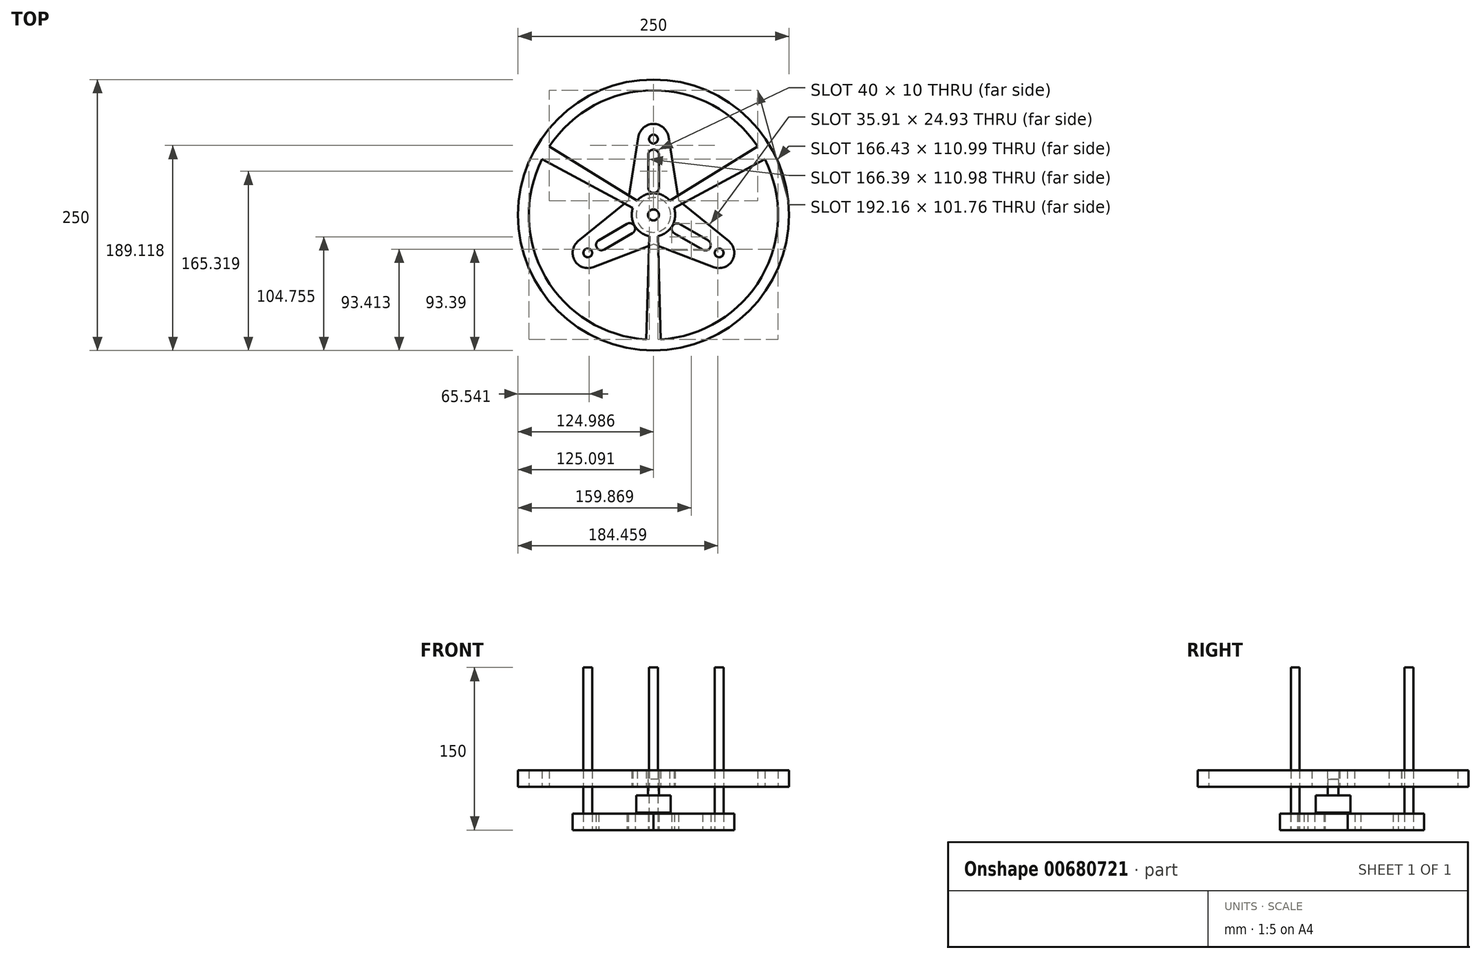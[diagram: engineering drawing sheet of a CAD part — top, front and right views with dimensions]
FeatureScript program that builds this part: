
annotation { "Feature Type Name" : "Feature", "Feature Type Description" : "" }
export const myFeature = defineFeature(function(context is Context, id is Id, definition is map)
    precondition{}
    {
        {
            var Q0;
            Q0=qCreatedBy(makeId("Top.planeOp"),FACE);
            var sketch = newSketch(context, id + "F0", { "sketchPlane" : qUnion([Q0])});
            skCircle(sketch, "E0", {"center": v(0, 70) * mm, "radius": 4 * mm});
            skCircle(sketch, "E1.1.0", {"center": v(-60.62, -35) * mm, "radius": 4 * mm});
            skCircle(sketch, "E1.2.0", {"center": v(60.62, -35) * mm, "radius": 4 * mm});
            skPoint(sketch, "E1.center", {"position": v(0, 0) * mm});
            skSolve(sketch);
        }
        {
            var Q0;
            Q0=makeQuery(id+"F0.imprint","IMPRINT",FACE,{"disambiguationData":[TD([[makeQuery(id+"F0.imprint","IMPRINT",EDGE,{"derivedFrom":sQuery(id+"F0.wireOp",EDGE,"E0")}),1.0]])]});
            var Q1;
            Q1=makeQuery(id+"F0.imprint","IMPRINT",FACE,{"disambiguationData":[TD([[makeQuery(id+"F0.imprint","IMPRINT",EDGE,{"derivedFrom":sQuery(id+"F0.wireOp",EDGE,"E1.1.0")}),1.0]])]});
            var Q2;
            Q2=makeQuery(id+"F0.imprint","IMPRINT",FACE,{"disambiguationData":[TD([[makeQuery(id+"F0.imprint","IMPRINT",EDGE,{"derivedFrom":sQuery(id+"F0.wireOp",EDGE,"E1.2.0")}),1.0]])]});
            extrude(context, id + "F1", {"entities" : qUnion([Q0, Q1, Q2]), "depth" : 150 * mm, "offsetDistance" : 25 * mm});
        }
        {
            var Q0;
            Q0=qCreatedBy(makeId("Top.planeOp"),FACE);
            var sketch = newSketch(context, id + "F2", { "sketchPlane" : qUnion([Q0])});
            skCircle(sketch, "E2", {"center": v(0, 0) * mm, "radius": 25 * mm});
            skCircle(sketch, "E3", {"center": v(0, 70) * mm, "radius": 14 * mm});
            skLineSegment(sketch, "E4", {"start": v(13.83, 72.2) * mm, "end": v(24.69, 3.93) * mm});
            skCircle(sketch, "E5", {"center": v(0, 70) * mm, "radius": 4.1 * mm});
            skLineSegment(sketch, "E6.MirrorCS", {"start": v(-13.83, 72.2) * mm, "end": v(-24.69, 3.93) * mm});
            skCircle(sketch, "E7.1.0", {"center": v(-60.62, -35) * mm, "radius": 14 * mm});
            skCircle(sketch, "E7.1.1", {"center": v(-60.62, -35) * mm, "radius": 4.1 * mm});
            skLineSegment(sketch, "E7.1.2", {"start": v(-55.61, -48.07) * mm, "end": v(8.94, -23.35) * mm});
            skLineSegment(sketch, "E7.1.3", {"start": v(-69.44, -24.13) * mm, "end": v(-15.75, 19.42) * mm});
            skCircle(sketch, "E7.2.0", {"center": v(60.62, -35) * mm, "radius": 14 * mm});
            skCircle(sketch, "E7.2.1", {"center": v(60.62, -35) * mm, "radius": 4.1 * mm});
            skLineSegment(sketch, "E7.2.2", {"start": v(69.44, -24.13) * mm, "end": v(15.75, 19.42) * mm});
            skLineSegment(sketch, "E7.2.3", {"start": v(55.61, -48.07) * mm, "end": v(-8.94, -23.35) * mm});
            skLineSegment(sketch, "E8", {"start": v(5.1, 55.44) * mm, "end": v(5.1, 25.44) * mm});
            skLineSegment(sketch, "E9", {"start": v(-4.9, 55.32) * mm, "end": v(-4.9, 25.32) * mm});
            skArc(sketch, "E10", {"start": v(-4.9, 55.32) * mm, "mid": v(0.03, 60.32) * mm, "end": v(5.1, 55.44) * mm});
            skArc(sketch, "E11", {"start": v(-4.9, 25.32) * mm, "mid": v(0.15, 20.32) * mm, "end": v(5.1, 25.44) * mm});
            skLineSegment(sketch, "E12.1.0", {"start": v(-45.45, -31.91) * mm, "end": v(-19.47, -16.91) * mm});
            skLineSegment(sketch, "E12.1.1", {"start": v(-50.56, -23.31) * mm, "end": v(-24.58, -8.31) * mm});
            skArc(sketch, "E12.1.2", {"start": v(-19.47, -16.91) * mm, "mid": v(-17.67, -10.03) * mm, "end": v(-24.58, -8.31) * mm});
            skArc(sketch, "E12.1.3", {"start": v(-45.45, -31.91) * mm, "mid": v(-52.25, -30.13) * mm, "end": v(-50.56, -23.31) * mm});
            skLineSegment(sketch, "E12.2.0", {"start": v(50.36, -23.4) * mm, "end": v(24.38, -8.4) * mm});
            skLineSegment(sketch, "E12.2.1", {"start": v(45.47, -32.13) * mm, "end": v(19.49, -17.13) * mm});
            skArc(sketch, "E12.2.2", {"start": v(24.38, -8.4) * mm, "mid": v(17.52, -10.3) * mm, "end": v(19.49, -17.13) * mm});
            skArc(sketch, "E12.2.3", {"start": v(50.36, -23.4) * mm, "mid": v(52.22, -30.19) * mm, "end": v(45.47, -32.13) * mm});
            skSolve(sketch);
        }
        {
            var Q0;
            {var subQ5=sQuery(id+"F2.wireOp",EDGE,"E9");Q0=makeQuery(id+"F2.imprint","IMPRINT",FACE,{"disambiguationData":[TD([[makeQuery(id+"F2.imprint","IMPRINT",EDGE,{"derivedFrom":subQ5}),-1.0]])]});}
            var Q1;
            Q1=makeQuery(id+"F2.imprint","IMPRINT",FACE,{"disambiguationData":[TD([[makeQuery(id+"F2.imprint","IMPRINT",EDGE,{"derivedFrom":sQuery(id+"F2.wireOp",EDGE,"E5")}),-1.0]])]});
            var Q2;
            {var subQ11=sQuery(id+"F2.wireOp",EDGE,"E8");Q2=makeQuery(id+"F2.imprint","IMPRINT",FACE,{"disambiguationData":[TD([[makeQuery(id+"F2.imprint","IMPRINT",EDGE,{"derivedFrom":subQ11}),1.0]])]});}
            var Q3;
            {var subQ0=sQuery(id+"F2.wireOp",EDGE,"E2");var subQ9=makeQuery(id+"F2.imprint","INTERSECT",VERTEX,{"derivedFrom":[subQ0,sQuery(id+"F2.wireOp",EDGE,"E4")]});Q3=makeQuery(id+"F2.imprint","IMPRINT",FACE,{"disambiguationData":[TD([[makeQuery(id+"F2.imprint","IMPRINT",EDGE,{"disambiguationData":[TD([[subQ9,-1.0]])],"derivedFrom":subQ0}),1.0]])]});}
            var Q4;
            {var subQ11=sQuery(id+"F2.wireOp",EDGE,"E12.1.1");Q4=makeQuery(id+"F2.imprint","IMPRINT",FACE,{"disambiguationData":[TD([[makeQuery(id+"F2.imprint","IMPRINT",EDGE,{"derivedFrom":subQ11}),1.0]])]});}
            var Q5;
            Q5=makeQuery(id+"F2.imprint","IMPRINT",FACE,{"disambiguationData":[TD([[makeQuery(id+"F2.imprint","IMPRINT",EDGE,{"derivedFrom":sQuery(id+"F2.wireOp",EDGE,"E7.1.1")}),-1.0]])]});
            var Q6;
            {var subQ6=sQuery(id+"F2.wireOp",EDGE,"E12.1.0");Q6=makeQuery(id+"F2.imprint","IMPRINT",FACE,{"disambiguationData":[TD([[makeQuery(id+"F2.imprint","IMPRINT",EDGE,{"derivedFrom":subQ6}),-1.0]])]});}
            var Q7;
            {var subQ8=sQuery(id+"F2.wireOp",EDGE,"E12.2.1");Q7=makeQuery(id+"F2.imprint","IMPRINT",FACE,{"disambiguationData":[TD([[makeQuery(id+"F2.imprint","IMPRINT",EDGE,{"derivedFrom":subQ8}),1.0]])]});}
            var Q8;
            {var subQ6=sQuery(id+"F2.wireOp",EDGE,"E12.2.0");Q8=makeQuery(id+"F2.imprint","IMPRINT",FACE,{"disambiguationData":[TD([[makeQuery(id+"F2.imprint","IMPRINT",EDGE,{"derivedFrom":subQ6}),-1.0]])]});}
            var Q9;
            Q9=makeQuery(id+"F2.imprint","IMPRINT",FACE,{"disambiguationData":[TD([[makeQuery(id+"F2.imprint","IMPRINT",EDGE,{"derivedFrom":sQuery(id+"F2.wireOp",EDGE,"E7.2.1")}),-1.0]])]});
            var Q10;
            {var subQ0=sQuery(id+"F2.wireOp",EDGE,"E4");var subQ1=sQuery(id+"F2.wireOp",EDGE,"E2");var subQ2=makeQuery(id+"F2.imprint","INTERSECT",VERTEX,{"derivedFrom":[subQ1,subQ0]});Q10=makeQuery(id+"F2.imprint","IMPRINT",FACE,{"disambiguationData":[TD([[makeQuery(id+"F2.imprint","IMPRINT",EDGE,{"disambiguationData":[TD([[subQ2,-1.0]])],"derivedFrom":subQ1}),-1.0]])]});}
            var Q11;
            {var subQ0=sQuery(id+"F2.wireOp",EDGE,"E6.MirrorCS");var subQ1=sQuery(id+"F2.wireOp",EDGE,"E2");var subQ2=makeQuery(id+"F2.imprint","INTERSECT",VERTEX,{"derivedFrom":[subQ1,subQ0]});Q11=makeQuery(id+"F2.imprint","IMPRINT",FACE,{"disambiguationData":[TD([[makeQuery(id+"F2.imprint","IMPRINT",EDGE,{"disambiguationData":[TD([[subQ2,1.0]])],"derivedFrom":subQ1}),-1.0]])]});}
            var Q12;
            {var subQ0=sQuery(id+"F2.wireOp",EDGE,"E7.1.2");var subQ1=sQuery(id+"F2.wireOp",EDGE,"E2");var subQ2=makeQuery(id+"F2.imprint","INTERSECT",VERTEX,{"derivedFrom":[subQ1,subQ0]});Q12=makeQuery(id+"F2.imprint","IMPRINT",FACE,{"disambiguationData":[TD([[makeQuery(id+"F2.imprint","IMPRINT",EDGE,{"disambiguationData":[TD([[subQ2,1.0]])],"derivedFrom":subQ1}),-1.0]])]});}
            extrude(context, id + "F3", {"entities" : qUnion([Q0, Q1, Q2, Q3, Q4, Q5, Q6, Q7, Q8, Q9, Q10, Q11, Q12]), "depth" : 15 * mm, "offsetDistance" : 25 * mm});
        }
        {
            var Q0;
            Q0=makeQuery(id+"F3.opExtrude","CAP_FACE",FACE,{"disambiguationData":[OSD([sQuery(id+"F2.wireOp",EDGE,"2h74rHo3-R582-kZou-qAnR-CPbRvHbkdvy5"),sQuery(id+"F2.wireOp",EDGE,"E3"),sQuery(id+"F2.wireOp",EDGE,"E4"),sQuery(id+"F2.wireOp",EDGE,"E5"),sQuery(id+"F2.wireOp",EDGE,"E6.MirrorCS"),sQuery(id+"F2.wireOp",EDGE,"E7.1.0"),sQuery(id+"F2.wireOp",EDGE,"E7.1.1"),sQuery(id+"F2.wireOp",EDGE,"E7.1.2"),sQuery(id+"F2.wireOp",EDGE,"E7.1.3"),sQuery(id+"F2.wireOp",EDGE,"E7.2.0"),sQuery(id+"F2.wireOp",EDGE,"E7.2.1"),sQuery(id+"F2.wireOp",EDGE,"E7.2.2"),sQuery(id+"F2.wireOp",EDGE,"E7.2.3")])],"isStart":false});
            cPlane(context, id + "F4", {"entities" : qUnion([Q0]), "cplaneType" : CPlaneType.OFFSET, "offset" : 25 * mm, "width" : 150 * mm, "height" : 150 * mm});
        }
        {
            var Q0;
            Q0=qCreatedBy(id+"F4.planeOp",FACE);
            var sketch = newSketch(context, id + "F5", { "sketchPlane" : qUnion([Q0])});
            skCircle(sketch, "E13", {"center": v(0, 0) * mm, "radius": 115 * mm});
            skCircle(sketch, "E14", {"center": v(0, 0) * mm, "radius": 125 * mm});
            skCircle(sketch, "E15", {"center": v(0, 0) * mm, "radius": 20 * mm});
            skLineSegment(sketch, "E16", {"start": v(-96.1, 63.18) * mm, "end": v(-15, 13.24) * mm});
            skLineSegment(sketch, "E17.MirrorCS", {"start": v(-102.78, 51.59) * mm, "end": v(-18.96, 6.37) * mm});
            skLineSegment(sketch, "E18.1.0", {"start": v(-6.67, -114.8) * mm, "end": v(-3.97, -19.6) * mm});
            skLineSegment(sketch, "E18.1.1", {"start": v(6.72, -114.8) * mm, "end": v(3.97, -19.6) * mm});
            skLineSegment(sketch, "E18.2.0", {"start": v(102.76, 51.63) * mm, "end": v(18.96, 6.37) * mm});
            skLineSegment(sketch, "E18.2.1", {"start": v(96.07, 63.22) * mm, "end": v(15, 13.24) * mm});
            skSolve(sketch);
        }
        {
            var Q0;
            Q0=makeQuery(id+"F5.imprint","IMPRINT",FACE,{"disambiguationData":[TD([[makeQuery(id+"F5.imprint","IMPRINT",EDGE,{"derivedFrom":sQuery(id+"F5.wireOp",EDGE,"E14")}),1.0]])]});
            var Q1;
            {var subQ0=sQuery(id+"F5.wireOp",EDGE,"E16");Q1=makeQuery(id+"F5.imprint","IMPRINT",FACE,{"disambiguationData":[TD([[makeQuery(id+"F5.imprint","IMPRINT",EDGE,{"derivedFrom":subQ0}),-1.0]])]});}
            var Q2;
            {var subQ0=sQuery(id+"F5.wireOp",EDGE,"E18.2.0");Q2=makeQuery(id+"F5.imprint","IMPRINT",FACE,{"disambiguationData":[TD([[makeQuery(id+"F5.imprint","IMPRINT",EDGE,{"derivedFrom":subQ0}),-1.0]])]});}
            var Q3;
            {var subQ0=sQuery(id+"F5.wireOp",EDGE,"E18.1.0");Q3=makeQuery(id+"F5.imprint","IMPRINT",FACE,{"disambiguationData":[TD([[makeQuery(id+"F5.imprint","IMPRINT",EDGE,{"derivedFrom":subQ0}),-1.0]])]});}
            var Q4;
            Q4=makeQuery(id+"F5.imprint","IMPRINT",FACE,{"disambiguationData":[TD([[makeQuery(id+"F5.imprint","IMPRINT",EDGE,{"derivedFrom":sQuery(id+"F5.wireOp",EDGE,"a9ee93d1-083a-4dbe-b281-c45d11f9854e")}),-1.0]])]});
            var Q5;
            {var subQ0=sQuery(id+"F5.wireOp",EDGE,"E15");var subQ5=makeQuery(id+"F5.imprint","INTERSECT",VERTEX,{"derivedFrom":[subQ0,sQuery(id+"F5.wireOp",EDGE,"E18.2.0")]});Q5=makeQuery(id+"F5.imprint","IMPRINT",FACE,{"disambiguationData":[TD([[makeQuery(id+"F5.imprint","IMPRINT",EDGE,{"disambiguationData":[TD([[subQ5,-1.0]])],"derivedFrom":subQ0}),1.0]])]});}
            extrude(context, id + "F6", {"entities" : qUnion([Q0, Q1, Q2, Q3, Q4, Q5]), "depth" : 15 * mm, "offsetDistance" : 25 * mm});
        }
        {
            var Q0;
            Q0=sQuery(id+"F2.wireOp",VERTEX,"E2.center");
            var Q1;
            Q1=makeQuery(id+"F6.opExtrude","SWEPT_BODY",BODY,{"disambiguationData":[OSD([sQuery(id+"F5.wireOp",EDGE,"E13"),sQuery(id+"F5.wireOp",EDGE,"E14"),sQuery(id+"F5.wireOp",EDGE,"E15"),sQuery(id+"F5.wireOp",EDGE,"E16"),sQuery(id+"F5.wireOp",EDGE,"E17.MirrorCS"),sQuery(id+"F5.wireOp",EDGE,"E18.1.0"),sQuery(id+"F5.wireOp",EDGE,"E18.1.1"),sQuery(id+"F5.wireOp",EDGE,"E18.2.0"),sQuery(id+"F5.wireOp",EDGE,"E18.2.1")])]});
            hole(context, id + "F7", {"style" : HoleStyle.SIMPLE, "endStyle" : HoleEndStyle.THROUGH, "oppositeDirection" : true, "holeDiameter" : 10.2 * mm, "majorDiameter" : 5 * mm, "isTappedThrough" : true, "tappedDepth" : 12 * mm, "tapClearance" : 3, "locations" : qUnion([Q0]), "scope" : qUnion([Q1])});
        }
        {
            var Q0;
            Q0=makeQuery(id+"F3.opExtrude","CAP_FACE",FACE,{"disambiguationData":[OSD([sQuery(id+"F2.wireOp",EDGE,"E3"),sQuery(id+"F2.wireOp",EDGE,"E4"),sQuery(id+"F2.wireOp",EDGE,"E5"),sQuery(id+"F2.wireOp",EDGE,"E6.MirrorCS"),sQuery(id+"F2.wireOp",EDGE,"E7.1.0"),sQuery(id+"F2.wireOp",EDGE,"E7.1.1"),sQuery(id+"F2.wireOp",EDGE,"E7.1.2"),sQuery(id+"F2.wireOp",EDGE,"E7.1.3"),sQuery(id+"F2.wireOp",EDGE,"E7.2.0"),sQuery(id+"F2.wireOp",EDGE,"E7.2.1"),sQuery(id+"F2.wireOp",EDGE,"E7.2.2"),sQuery(id+"F2.wireOp",EDGE,"E7.2.3"),sQuery(id+"F2.wireOp",EDGE,"E8"),sQuery(id+"F2.wireOp",EDGE,"E9"),sQuery(id+"F2.wireOp",EDGE,"E10"),sQuery(id+"F2.wireOp",EDGE,"E11"),sQuery(id+"F2.wireOp",EDGE,"E12.1.0"),sQuery(id+"F2.wireOp",EDGE,"E12.1.1"),sQuery(id+"F2.wireOp",EDGE,"E12.1.2"),sQuery(id+"F2.wireOp",EDGE,"E12.1.3"),sQuery(id+"F2.wireOp",EDGE,"E12.2.0"),sQuery(id+"F2.wireOp",EDGE,"E12.2.1"),sQuery(id+"F2.wireOp",EDGE,"E12.2.2"),sQuery(id+"F2.wireOp",EDGE,"E12.2.3")])],"isStart":false});
            cPlane(context, id + "F8", {"entities" : qUnion([Q0]), "cplaneType" : CPlaneType.OFFSET, "offset" : 1 * mm, "width" : 150 * mm, "height" : 150 * mm});
        }
        {
            var Q0;
            Q0=qCreatedBy(id+"F8.planeOp",FACE);
            var sketch = newSketch(context, id + "F9", { "sketchPlane" : qUnion([Q0])});
            skCircle(sketch, "E19", {"center": v(0, 0) * mm, "radius": 16 * mm});
            skSolve(sketch);
        }
        {
            var Q0;
            Q0=makeQuery(id+"F9.imprint","IMPRINT",FACE,{"disambiguationData":[TD([[makeQuery(id+"F9.imprint","IMPRINT",EDGE,{"derivedFrom":sQuery(id+"F9.wireOp",EDGE,"E19")}),1.0]])]});
            extrude(context, id + "F10", {"entities" : qUnion([Q0]), "depth" : 16 * mm, "offsetDistance" : 25 * mm});
        }
        {
            var Q0;
            Q0=makeQuery(id+"F10.opExtrude","CAP_FACE",FACE,{"disambiguationData":[OSD([sQuery(id+"F9.wireOp",EDGE,"E19")])],"isStart":false});
            var sketch = newSketch(context, id + "F11", { "sketchPlane" : qUnion([Q0])});
            skCircle(sketch, "E20", {"center": v(0, 0) * mm, "radius": 5 * mm});
            skSolve(sketch);
        }
        {
            var Q0;
            Q0=makeQuery(id+"F11.imprint","IMPRINT",FACE,{"disambiguationData":[TD([[makeQuery(id+"F11.imprint","IMPRINT",EDGE,{"derivedFrom":sQuery(id+"F11.wireOp",EDGE,"E20")}),1.0]])]});
            extrude(context, id + "F12", {"entities" : qUnion([Q0]), "operationType" : NewBodyOperationType.ADD, "depth" : 15 * mm, "offsetDistance" : 25 * mm});
        }
    });
